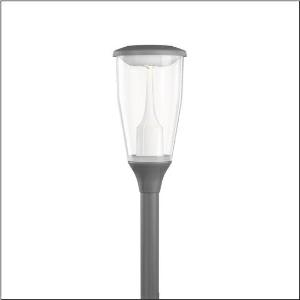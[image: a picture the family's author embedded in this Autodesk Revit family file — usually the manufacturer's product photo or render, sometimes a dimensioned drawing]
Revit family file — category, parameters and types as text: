
# Revit family: dl_11_iq___p1_0a_5xa5565nf14hp00022_fef3
name_source: partatom
category: Lighting Fixtures
units: mm (PartAtom-declared; Revit-internal decimal feet)

## family parameters
Cut with Voids When Loaded = No
Host = Face
Light Source = No
Part Type = Normal
Room Calculation Point = No
Round Connector Dimension = Use Diameter
Shared = No

## types (1)
- --- (1 x LED, 4280 lm, 33.6 W, 2700K)
    Apparent Load = 34 VA
    CIE Flux Codes = 23 60 93 95 100
    Color Rendering = 70
    Color Temperature = 2700K
    Default Elevation = 1800 mm
    Description = DL 11 iQ, mast luminaire, Module 540 iQ-SR, primary light control with 3 zone facetted reflector, of plastic, silver coated, highly specular, structured, primary optical cover: cover, of PMMA, transparent, light distribution: P1.0a, light emission: direct distribution, primary light characteristic: asymmetric, installation type: post-top, LED, High Power LED, light colour: 727, colour temperature: 2700K, control: Street-Remote, Auto-Match, Temp-Guard, Lumen-Switch, Night-Set, Smart-Wire, Light-Fading, Desk-Remote (wireless, voltage-free reading and setting of iQ features in the workshop via application-optimized NFC function/RFID function), optimised constant luminous flux control (CLO 2.0), mains connection: 220..240V, AC, 50/60Hz, connection cable pre-assembled, cable length: 5,5m, start of lifetime: 34W, end of service life: 36W, luminaire housing, upper part, of diecast aluminium, coated, Siteco® metallic grey (DB 702S), spigot size: 60mm (post-top), post-top mast mounting element, of diecast aluminium, coated, Siteco® metallic grey (DB 702S), Module 540 iQ-SR, traffic white (RAL 9016), equipment: Power, protection rating (complete): IP66, insulation class (complete): insulation class II (safety insulation), certification: CE, ENEC, ENEC+, VDE, packaging unit: 1 piece

Light Distribution: P1.0a
    Height = 665 mm
    Lamp = 1 x LED
    Lamp Light Flux = 4280 lm
    Lamp Power = 33.6 W
    Lamp count = 1
    Length = 334 mm
    Luminous efficacy = 127 lm/W
    Manufacturer = Siteco
    ModVariant = No
    Model = 5XA5565NF14HP00022
    Number of Poles = 1
    OnlyDefault = Yes
    Power Factor = 1
    Product Name = DL 11 iQ | P1.0a
    Product group = mast luminaire | pylon top
    ProductGroupID = 6100
    Protection Class = Protection class II
    Protection Degree = IP 66
    RLX_Detail_Level = 1
    RLX_Emergency_Light_Flux = 0 lm
    RLX_Emergency_Type = 0
    RLX_Emergency_Type_DB = No
    RlxData = <blob elided: 103953 chars, md5=db3b8a13>
    Socket = socket
    Standby Power = 0 W
    System Light Flux = 4280 lm
    System Power = 34 W
    Type Comments = factory setting: luminous flux: 100 % | dim-lin: 254 | 695 mA
    Type Image = l_1258354.jpg
    URL = http://relux.com
    VarID = @adj_021897
    Voltage = 0 V
    Weight = 0.00 kg
    Width = 0 mm  [stored 0 ft]

note: [stored X ft] marks values corroborated as IEEE doubles in the binary element streams (Revit-internal decimal feet)

## geometry (parser evidence)
native form markers: Blend x4, Sweep x10
no freeform markers — native parametric forms only
